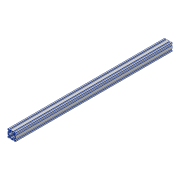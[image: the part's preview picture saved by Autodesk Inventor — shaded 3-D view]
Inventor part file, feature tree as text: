
AUTODESK INVENTOR PART (.ipt)
format: ipt  version: 2018 (Build 220112000, 112)  size: 299,520 bytes
history: native  units: mm
features: extrude x1, sketch x1
ambient origin geometry x8: Origin, YZ Plane, XZ Plane, XY Plane, X Axis, Y Axis, Z Axis, Center Point
bodies: Solid1 (feature_tree)
feature tree (2):
  extrude  "Extrusion1"  [1 undecoded]
  sketch  "Sketch1"  dims[d0=800.0mm d1=0.0mm]
note: 1 required parameter value undecoded (feature->parameter linkage not recoverable at this tier; creation-order binding heuristic only, values carry confidence <= 0.55)
